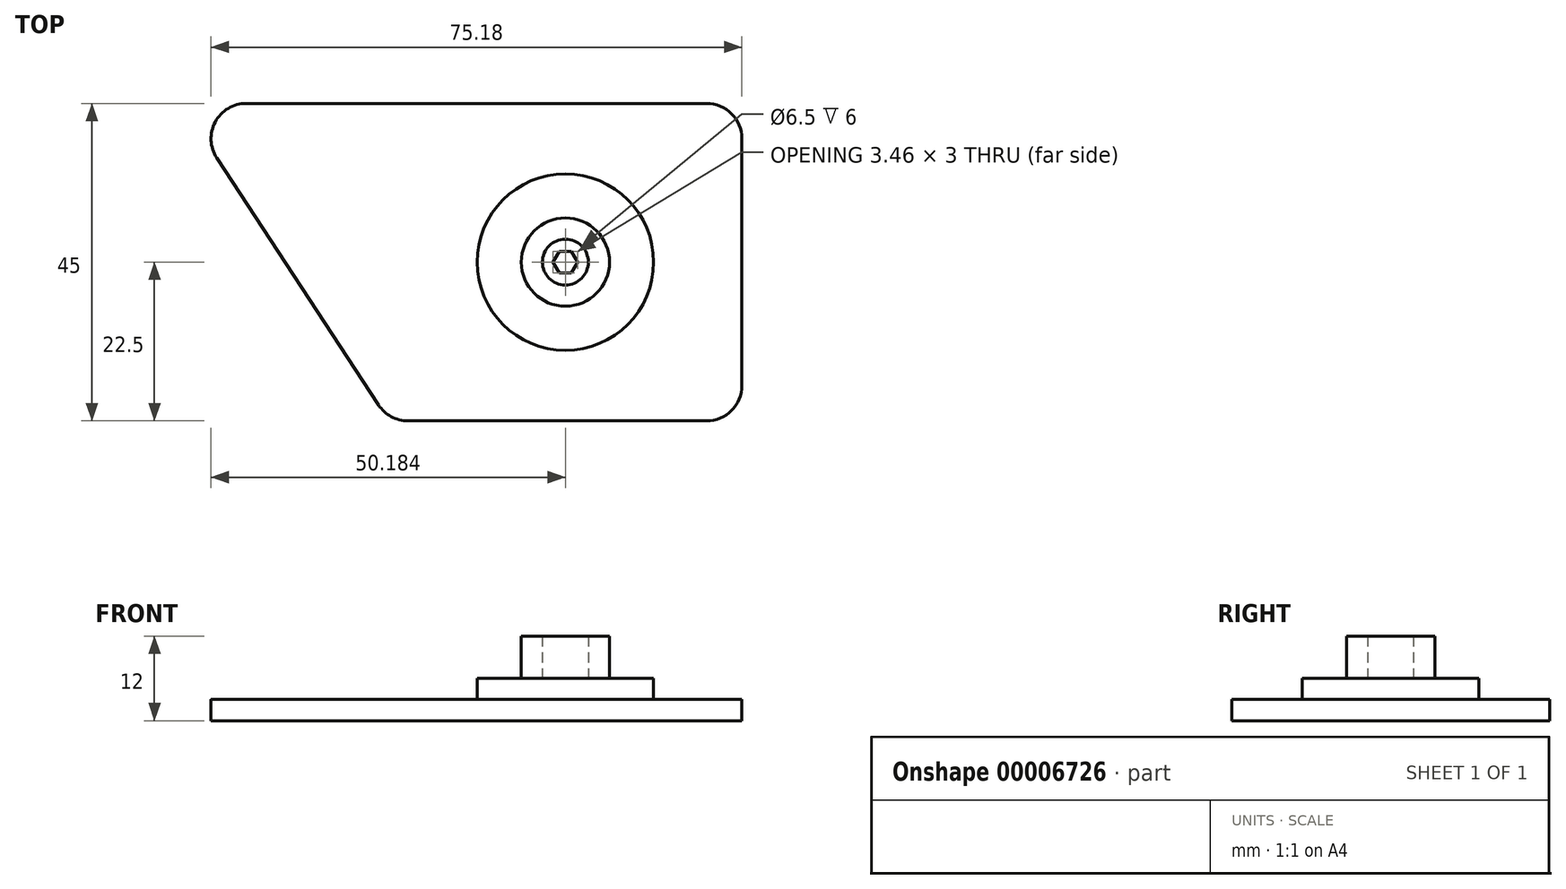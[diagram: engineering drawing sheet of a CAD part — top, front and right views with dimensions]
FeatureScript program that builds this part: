
annotation { "Feature Type Name" : "Feature", "Feature Type Description" : "" }
export const myFeature = defineFeature(function(context is Context, id is Id, definition is map)
    precondition{}
    {
        {
            var Q0;
            Q0=qCreatedBy(makeId("Top.planeOp"),FACE);
            var sketch = newSketch(context, id + "F0", { "sketchPlane" : qUnion([Q0])});
            skLineSegment(sketch, "E0", {"start": v(37.6, -5) * mm, "end": v(37.6, -45) * mm});
            skLineSegment(sketch, "E1", {"start": v(37.6, -45) * mm, "end": v(-12.4, -45) * mm});
            skLineSegment(sketch, "E2", {"start": v(-12.4, -45) * mm, "end": v(-36.78, -7.74) * mm});
            skLineSegment(sketch, "E3", {"start": v(32.6, 0) * mm, "end": v(-32.6, 0) * mm});
            skPoint(sketch, "E4.visualSharp", {"position": v(-41.84, 0) * mm});
            skArc(sketch, "E4.filletArc", {"start": v(-32.6, 0) * mm, "mid": v(-37, -2.62) * mm, "end": v(-36.78, -7.74) * mm});
            skPoint(sketch, "E5.visualSharp", {"position": v(37.6, 0) * mm});
            skArc(sketch, "E5.filletArc", {"start": v(37.6, -5) * mm, "mid": v(36.13, -1.46) * mm, "end": v(32.6, 0) * mm});
            skSolve(sketch);
        }
        {
            var Q0;
            Q0=makeQuery(id+"F0.imprint","IMPRINT",FACE,{"disambiguationData":[TD([[makeQuery(id+"F0.imprint","IMPRINT",EDGE,{"derivedFrom":sQuery(id+"F0.wireOp",EDGE,"E0")}),-1.0]])]});
            extrude(context, id + "F1", {"entities" : qUnion([Q0]), "depth" : 3 * mm});
        }
        {
            var Q0;
            Q0=qCreatedBy(makeId("Top.planeOp"),FACE);
            var sketch = newSketch(context, id + "F2", { "sketchPlane" : qUnion([Q0])});
            skCircle(sketch, "E6", {"center": v(12.6, -22.5) * mm, "radius": 12.5 * mm});
            skSolve(sketch);
        }
        {
            var Q0;
            Q0=qSketchRegion(id+"F2",true);
            var Q1;
            Q1=sQuery(id+"F2.wireOp",EDGE,"E6");
            extrude(context, id + "F3", {"entities" : qUnion([Q0]), "operationType" : NewBodyOperationType.ADD, "surfaceEntities" : qUnion([Q1]), "depth" : 6 * mm});
        }
        {
            var Q0;
            Q0=makeQuery(id+"F1.opExtrude","SWEPT_EDGE",EDGE,{"disambiguationData":[OSD([sQuery(id+"F0.wireOp",EDGE,"E0"),sQuery(id+"F0.wireOp",EDGE,"E3")])]});
            fillet(context, id + "F4", {"entities" : qUnion([Q0]), "radius" : 5 * mm, "tangentPropagation" : true, "allowEdgeOverflow" : false});
        }
        {
            var Q0;
            Q0=makeQuery(id+"F1.opExtrude","SWEPT_EDGE",EDGE,{"disambiguationData":[OSD([sQuery(id+"F0.wireOp",EDGE,"E1"),sQuery(id+"F0.wireOp",EDGE,"E2")])]});
            fillet(context, id + "F5", {"entities" : qUnion([Q0]), "radius" : 5 * mm, "tangentPropagation" : true, "allowEdgeOverflow" : false});
        }
        {
            var Q0;
            Q0=makeQuery(id+"F3.opExtrude","CAP_FACE",FACE,{"disambiguationData":[OSD([sQuery(id+"F2.wireOp",EDGE,"E6")])],"isStart":false});
            var sketch = newSketch(context, id + "F6", { "sketchPlane" : qUnion([Q0])});
            skCircle(sketch, "E7", {"center": v(12.6, -22.5) * mm, "radius": 6.25 * mm});
            skCircle(sketch, "E8.0", {"center": v(12.6, -22.5) * mm, "radius": 3.25 * mm});
            skSolve(sketch);
        }
        {
            var Q0;
            Q0 = qSketchRegion(id + "F6", true);
            extrude(context, id + "F7", {"entities" : qUnion([Q0]), "operationType" : NewBodyOperationType.ADD, "depth" : 6 * mm});
        }
        {
            var Q0;
            Q0=makeQuery(id+"F7.boolean.opBoolean","SPLIT",FACE,{"disambiguationData":[TD([makeQuery(id+"F7.opExtrude","SWEPT_FACE",FACE,{"disambiguationData":[OSD([sQuery(id+"F6.wireOp",EDGE,"E8.0")])]})])],"derivedFrom":makeQuery(id+"F3.opExtrude","CAP_FACE",FACE,{"disambiguationData":[OSD([sQuery(id+"F2.wireOp",EDGE,"E6")])],"isStart":false})});
            var sketch = newSketch(context, id + "F8", { "sketchPlane" : qUnion([Q0])});
            skCircle(sketch, "E9.cCircle", {"center": v(12.6, -22.5) * mm, "radius": 1.5 * mm, "construction": true});
            skLineSegment(sketch, "E9.0", {"start": v(13.46, -24) * mm, "end": v(11.73, -24) * mm});
            skLineSegment(sketch, "E9.1", {"start": v(11.73, -24) * mm, "end": v(10.86, -22.5) * mm});
            skLineSegment(sketch, "E9.2", {"start": v(10.86, -22.5) * mm, "end": v(11.73, -21) * mm});
            skLineSegment(sketch, "E9.3", {"start": v(11.73, -21) * mm, "end": v(13.46, -21) * mm});
            skLineSegment(sketch, "E9.4", {"start": v(13.46, -21) * mm, "end": v(14.33, -22.5) * mm});
            skLineSegment(sketch, "E9.5", {"start": v(14.33, -22.5) * mm, "end": v(13.46, -24) * mm});
            skPoint(sketch, "E9.0.midPoint", {"position": v(12.6, -24) * mm});
            skSolve(sketch);
        }
        {
            var Q0;
            Q0=makeQuery(id+"F8.imprint","IMPRINT",FACE,{"disambiguationData":[TD([[makeQuery(id+"F8.imprint","IMPRINT",EDGE,{"derivedFrom":sQuery(id+"F8.wireOp",EDGE,"E9.0")}),-1.0]])]});
            extrude(context, id + "F9", {"entities" : qUnion([Q0]), "operationType" : NewBodyOperationType.REMOVE, "oppositeDirection" : true, "depth" : 12 * mm});
        }
    });
